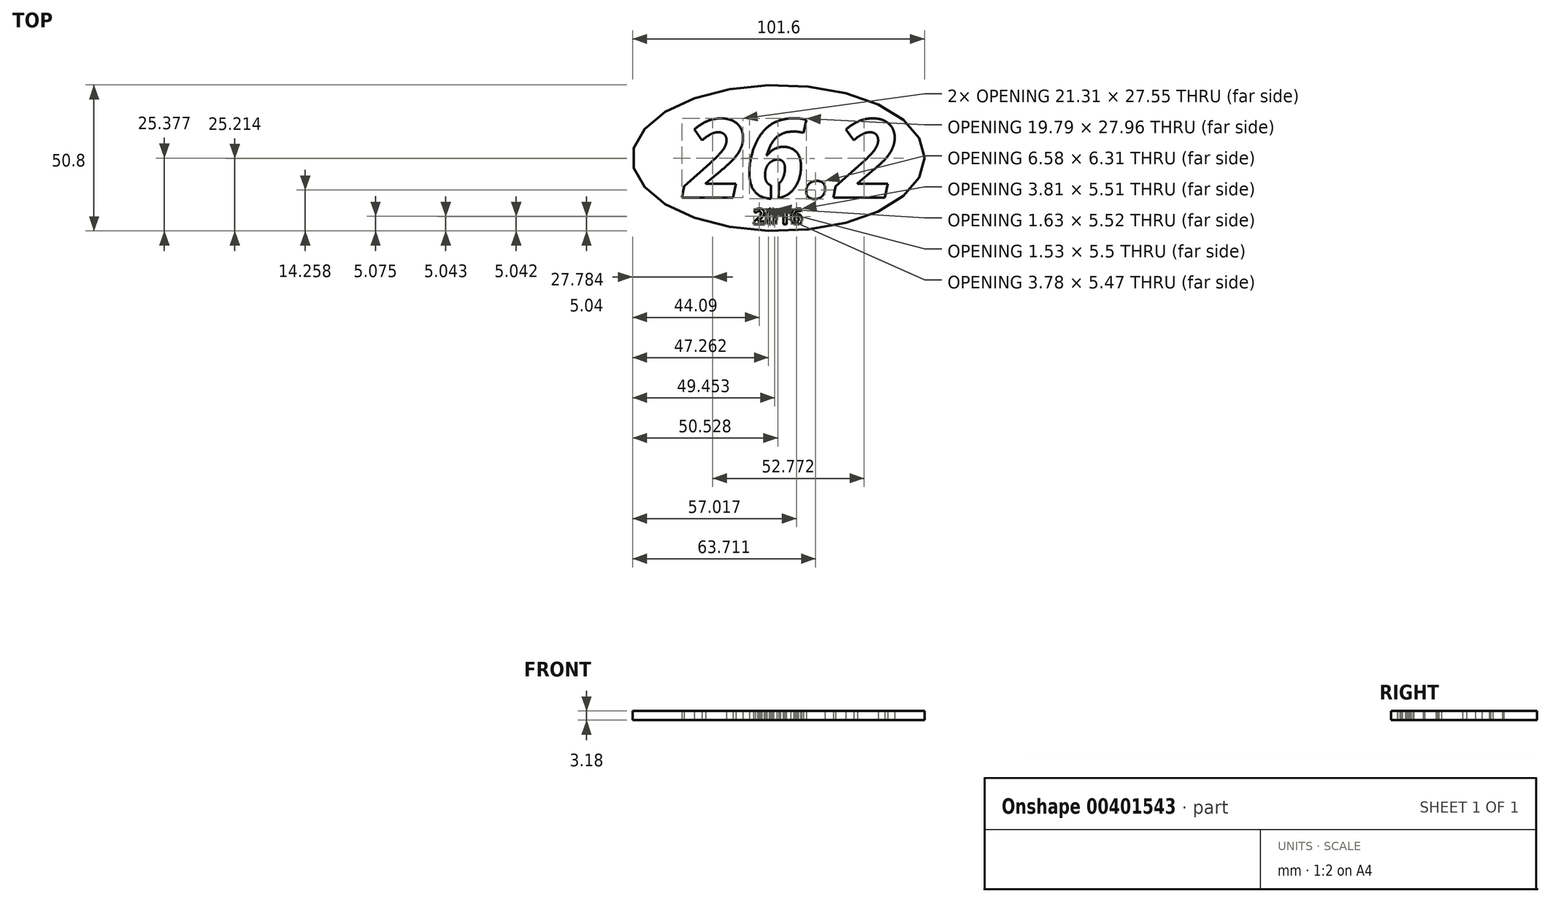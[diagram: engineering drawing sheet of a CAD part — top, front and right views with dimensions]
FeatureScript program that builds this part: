
annotation { "Feature Type Name" : "Feature", "Feature Type Description" : "" }
export const myFeature = defineFeature(function(context is Context, id is Id, definition is map)
    precondition{}
    {
        {
            var Q0;
            Q0=qCreatedBy(makeId("Top.planeOp"),FACE);
            var sketch = newSketch(context, id + "F0", { "sketchPlane" : qUnion([Q0])});
            skEllipse(sketch, "E0", {"center": v(0, 0) * mm, "majorRadius": 50.8 * mm, "minorRadius": 25.4 * mm, "majorAxis": v(1, 0)});
            skText(sketch, "E1", { "text": " 26.2", "fontName": "OpenSans-BoldItalic.ttf"});
            skLineSegment(sketch, "E2", {"start": v(-2.64, -9.19) * mm, "end": v(-2.64, -15.13) * mm});
            skLineSegment(sketch, "E3", {"start": v(-2.64, -15.13) * mm, "end": v(0, -15.13) * mm});
            skLineSegment(sketch, "E4", {"start": v(0, -15.13) * mm, "end": v(0.12, -8.69) * mm});
            skLineSegment(sketch, "E5", {"start": v(0.12, -8.69) * mm, "end": v(-2.64, -8.63) * mm});
            skLineSegment(sketch, "E6", {"start": v(-2.64, -8.63) * mm, "end": v(-2.64, -9.19) * mm});
            const initialGuessF0  = {"E1": [-0.04265, -0.0138, 1, 0, 0.0274]};
            skSetInitialGuess(sketch, initialGuessF0);
            skSolve(sketch);
        }
        {
            var Q0;
            Q0=makeQuery(id+"F0.imprint","IMPRINT",FACE,{"disambiguationData":[TD([[makeQuery(id+"F0.imprint","IMPRINT",EDGE,{"derivedFrom":sQuery(id+"F0.wireOp",EDGE,"E0")}),1.0]])]});
            var Q1;
            {var subQ5=sQuery(id+"F0.wireOp",EDGE,"E1.sketch_text.stroke-40");Q1=makeQuery(id+"F0.imprint","IMPRINT",FACE,{"disambiguationData":[TD([[makeQuery(id+"F0.imprint","IMPRINT",EDGE,{"derivedFrom":subQ5}),1.0]])]});}
            var Q2;
            {var subQ7=sQuery(id+"F0.wireOp",EDGE,"E1.sketch_text.stroke-37");var subQ8=sQuery(id+"F0.wireOp",EDGE,"E1.sketch_text.stroke-36");var subQ9=makeQuery(id+"F0.imprint","INTERSECT",VERTEX,{"derivedFrom":[subQ8,subQ7]});Q2=makeQuery(id+"F0.imprint","IMPRINT",FACE,{"disambiguationData":[TD([[makeQuery(id+"F0.imprint","IMPRINT",EDGE,{"disambiguationData":[TD([[subQ9,1.0]])],"derivedFrom":subQ8}),-1.0]])]});}
            var Q3;
            {var subQ0=sQuery(id+"F0.wireOp",EDGE,"E3");Q3=makeQuery(id+"F0.imprint","IMPRINT",FACE,{"disambiguationData":[TD([[makeQuery(id+"F0.imprint","IMPRINT",EDGE,{"derivedFrom":subQ0}),1.0]])]});}
            var Q4;
            {var subQ0=sQuery(id+"F0.wireOp",EDGE,"E5");Q4=makeQuery(id+"F0.imprint","IMPRINT",FACE,{"disambiguationData":[TD([[makeQuery(id+"F0.imprint","IMPRINT",EDGE,{"derivedFrom":subQ0}),1.0]])]});}
            extrude(context, id + "F1", {"entities" : qUnion([Q0, Q1, Q2, Q3, Q4]), "depth" : 3.17 * mm});
        }
        {
            var Q0;
            Q0=makeQuery(id+"F1.opExtrude","CAP_FACE",FACE,{"disambiguationData":[OSD([sQuery(id+"F0.wireOp",EDGE,"E0"),sQuery(id+"F0.wireOp",EDGE,"E1.sketch_text.stroke-0"),sQuery(id+"F0.wireOp",EDGE,"E1.sketch_text.stroke-1"),sQuery(id+"F0.wireOp",EDGE,"E1.sketch_text.stroke-2"),sQuery(id+"F0.wireOp",EDGE,"E1.sketch_text.stroke-3"),sQuery(id+"F0.wireOp",EDGE,"E1.sketch_text.stroke-4"),sQuery(id+"F0.wireOp",EDGE,"E1.sketch_text.stroke-5"),sQuery(id+"F0.wireOp",EDGE,"E1.sketch_text.stroke-6"),sQuery(id+"F0.wireOp",EDGE,"E1.sketch_text.stroke-7"),sQuery(id+"F0.wireOp",EDGE,"E1.sketch_text.stroke-8"),sQuery(id+"F0.wireOp",EDGE,"E1.sketch_text.stroke-9"),sQuery(id+"F0.wireOp",EDGE,"E1.sketch_text.stroke-10"),sQuery(id+"F0.wireOp",EDGE,"E1.sketch_text.stroke-11"),sQuery(id+"F0.wireOp",EDGE,"E1.sketch_text.stroke-12"),sQuery(id+"F0.wireOp",EDGE,"E1.sketch_text.stroke-13"),sQuery(id+"F0.wireOp",EDGE,"E1.sketch_text.stroke-14"),sQuery(id+"F0.wireOp",EDGE,"E1.sketch_text.stroke-15"),sQuery(id+"F0.wireOp",EDGE,"E1.sketch_text.stroke-16"),sQuery(id+"F0.wireOp",EDGE,"E1.sketch_text.stroke-17"),sQuery(id+"F0.wireOp",EDGE,"E1.sketch_text.stroke-18"),sQuery(id+"F0.wireOp",EDGE,"E1.sketch_text.stroke-19"),sQuery(id+"F0.wireOp",EDGE,"E1.sketch_text.stroke-20"),sQuery(id+"F0.wireOp",EDGE,"E1.sketch_text.stroke-21"),sQuery(id+"F0.wireOp",EDGE,"E1.sketch_text.stroke-22"),sQuery(id+"F0.wireOp",EDGE,"E1.sketch_text.stroke-23"),sQuery(id+"F0.wireOp",EDGE,"E1.sketch_text.stroke-24"),sQuery(id+"F0.wireOp",EDGE,"E1.sketch_text.stroke-25"),sQuery(id+"F0.wireOp",EDGE,"E1.sketch_text.stroke-26"),sQuery(id+"F0.wireOp",EDGE,"E1.sketch_text.stroke-27"),sQuery(id+"F0.wireOp",EDGE,"E1.sketch_text.stroke-28"),sQuery(id+"F0.wireOp",EDGE,"E1.sketch_text.stroke-29"),sQuery(id+"F0.wireOp",EDGE,"E1.sketch_text.stroke-30"),sQuery(id+"F0.wireOp",EDGE,"E1.sketch_text.stroke-31"),sQuery(id+"F0.wireOp",EDGE,"E1.sketch_text.stroke-32"),sQuery(id+"F0.wireOp",EDGE,"E1.sketch_text.stroke-33"),sQuery(id+"F0.wireOp",EDGE,"E1.sketch_text.stroke-34"),sQuery(id+"F0.wireOp",EDGE,"E1.sketch_text.stroke-35"),sQuery(id+"F0.wireOp",EDGE,"E1.sketch_text.stroke-36"),sQuery(id+"F0.wireOp",EDGE,"E1.sketch_text.stroke-37"),sQuery(id+"F0.wireOp",EDGE,"E1.sketch_text.stroke-38"),sQuery(id+"F0.wireOp",EDGE,"E1.sketch_text.stroke-39"),sQuery(id+"F0.wireOp",EDGE,"E1.sketch_text.stroke-40"),sQuery(id+"F0.wireOp",EDGE,"E1.sketch_text.stroke-41"),sQuery(id+"F0.wireOp",EDGE,"E1.sketch_text.stroke-42"),sQuery(id+"F0.wireOp",EDGE,"E1.sketch_text.stroke-43"),sQuery(id+"F0.wireOp",EDGE,"E1.sketch_text.stroke-44"),sQuery(id+"F0.wireOp",EDGE,"E1.sketch_text.stroke-45"),sQuery(id+"F0.wireOp",EDGE,"E1.sketch_text.stroke-46"),sQuery(id+"F0.wireOp",EDGE,"E1.sketch_text.stroke-47"),sQuery(id+"F0.wireOp",EDGE,"E1.sketch_text.stroke-48"),sQuery(id+"F0.wireOp",EDGE,"E1.sketch_text.stroke-49"),sQuery(id+"F0.wireOp",EDGE,"E1.sketch_text.stroke-50"),sQuery(id+"F0.wireOp",EDGE,"E1.sketch_text.stroke-51"),sQuery(id+"F0.wireOp",EDGE,"E1.sketch_text.stroke-52"),sQuery(id+"F0.wireOp",EDGE,"E1.sketch_text.stroke-53"),sQuery(id+"F0.wireOp",EDGE,"E1.sketch_text.stroke-54"),sQuery(id+"F0.wireOp",EDGE,"E1.sketch_text.stroke-55"),sQuery(id+"F0.wireOp",EDGE,"E1.sketch_text.stroke-56"),sQuery(id+"F0.wireOp",EDGE,"E1.sketch_text.stroke-57"),sQuery(id+"F0.wireOp",EDGE,"E1.sketch_text.stroke-58"),sQuery(id+"F0.wireOp",EDGE,"E1.sketch_text.stroke-59"),sQuery(id+"F0.wireOp",EDGE,"E1.sketch_text.stroke-60"),sQuery(id+"F0.wireOp",EDGE,"E1.sketch_text.stroke-61"),sQuery(id+"F0.wireOp",EDGE,"E1.sketch_text.stroke-62"),sQuery(id+"F0.wireOp",EDGE,"E1.sketch_text.stroke-63"),sQuery(id+"F0.wireOp",EDGE,"E1.sketch_text.stroke-64"),sQuery(id+"F0.wireOp",EDGE,"E1.sketch_text.stroke-65"),sQuery(id+"F0.wireOp",EDGE,"E1.sketch_text.stroke-66"),sQuery(id+"F0.wireOp",EDGE,"E1.sketch_text.stroke-67"),sQuery(id+"F0.wireOp",EDGE,"E1.sketch_text.stroke-68"),sQuery(id+"F0.wireOp",EDGE,"E1.sketch_text.stroke-69"),sQuery(id+"F0.wireOp",EDGE,"E1.sketch_text.stroke-70"),sQuery(id+"F0.wireOp",EDGE,"E1.sketch_text.stroke-71"),sQuery(id+"F0.wireOp",EDGE,"E1.sketch_text.stroke-72"),sQuery(id+"F0.wireOp",EDGE,"E1.sketch_text.stroke-73"),sQuery(id+"F0.wireOp",EDGE,"E1.sketch_text.stroke-74"),sQuery(id+"F0.wireOp",EDGE,"E1.sketch_text.stroke-75"),sQuery(id+"F0.wireOp",EDGE,"E1.sketch_text.stroke-76"),sQuery(id+"F0.wireOp",EDGE,"E2"),sQuery(id+"F0.wireOp",EDGE,"E4")])],"isStart":false});
            var sketch = newSketch(context, id + "F2", { "sketchPlane" : qUnion([Q0])});
            skText(sketch, "E7", { "text": "2016", "fontName": "OpenSans-Bold.ttf"});
            skLineSegment(sketch, "E8", {"start": v(-2.77, -17.19) * mm, "end": v(-2.77, -23.46) * mm});
            skLineSegment(sketch, "E9", {"start": v(-2.77, -23.46) * mm, "end": v(-2.16, -23.46) * mm});
            skLineSegment(sketch, "E10", {"start": v(-2.16, -23.46) * mm, "end": v(-2.16, -17.13) * mm});
            skLineSegment(sketch, "E11", {"start": v(-2.16, -17.13) * mm, "end": v(-2.77, -17.19) * mm});
            skLineSegment(sketch, "E12", {"start": v(6, -21.98) * mm, "end": v(6, -23.51) * mm});
            skLineSegment(sketch, "E13", {"start": v(6, -23.51) * mm, "end": v(6.7, -23.51) * mm});
            skLineSegment(sketch, "E14", {"start": v(6.7, -23.51) * mm, "end": v(6.7, -21.98) * mm});
            skLineSegment(sketch, "E15", {"start": v(6.7, -21.98) * mm, "end": v(6, -21.98) * mm});
            const initialGuessF2  = {"E7": [-0.00889, -0.02306, 1, 0, 0.00544]};
            skSetInitialGuess(sketch, initialGuessF2);
            skSolve(sketch);
        }
        {
            var Q0;
            Q0=makeQuery(id+"F2.imprint","IMPRINT",FACE,{"disambiguationData":[TD([[makeQuery(id+"F2.imprint","IMPRINT",EDGE,{"derivedFrom":sQuery(id+"F2.wireOp",EDGE,"E7.sketch_text.stroke-0")}),-1.0]])]});
            var Q1;
            {var subQ4=sQuery(id+"F2.wireOp",EDGE,"E7.sketch_text.stroke-27");Q1=makeQuery(id+"F2.imprint","IMPRINT",FACE,{"disambiguationData":[TD([[makeQuery(id+"F2.imprint","IMPRINT",EDGE,{"derivedFrom":subQ4}),-1.0]])]});}
            var Q2;
            {var subQ1=sQuery(id+"F2.wireOp",EDGE,"E7.sketch_text.stroke-24");Q2=makeQuery(id+"F2.imprint","IMPRINT",FACE,{"disambiguationData":[TD([[makeQuery(id+"F2.imprint","IMPRINT",EDGE,{"derivedFrom":subQ1}),-1.0]])]});}
            var Q3;
            Q3=makeQuery(id+"F2.imprint","IMPRINT",FACE,{"disambiguationData":[TD([[makeQuery(id+"F2.imprint","IMPRINT",EDGE,{"derivedFrom":sQuery(id+"F2.wireOp",EDGE,"E7.sketch_text.stroke-40")}),-1.0]])]});
            var Q4;
            Q4=makeQuery(id+"F2.imprint","IMPRINT",FACE,{"disambiguationData":[TD([[makeQuery(id+"F2.imprint","IMPRINT",EDGE,{"derivedFrom":sQuery(id+"F2.wireOp",EDGE,"E7.sketch_text.stroke-50")}),-1.0]])]});
            extrude(context, id + "F3", {"entities" : qUnion([Q0, Q1, Q2, Q3, Q4]), "operationType" : NewBodyOperationType.REMOVE, "oppositeDirection" : true, "depth" : 3.17 * mm});
        }
    });
